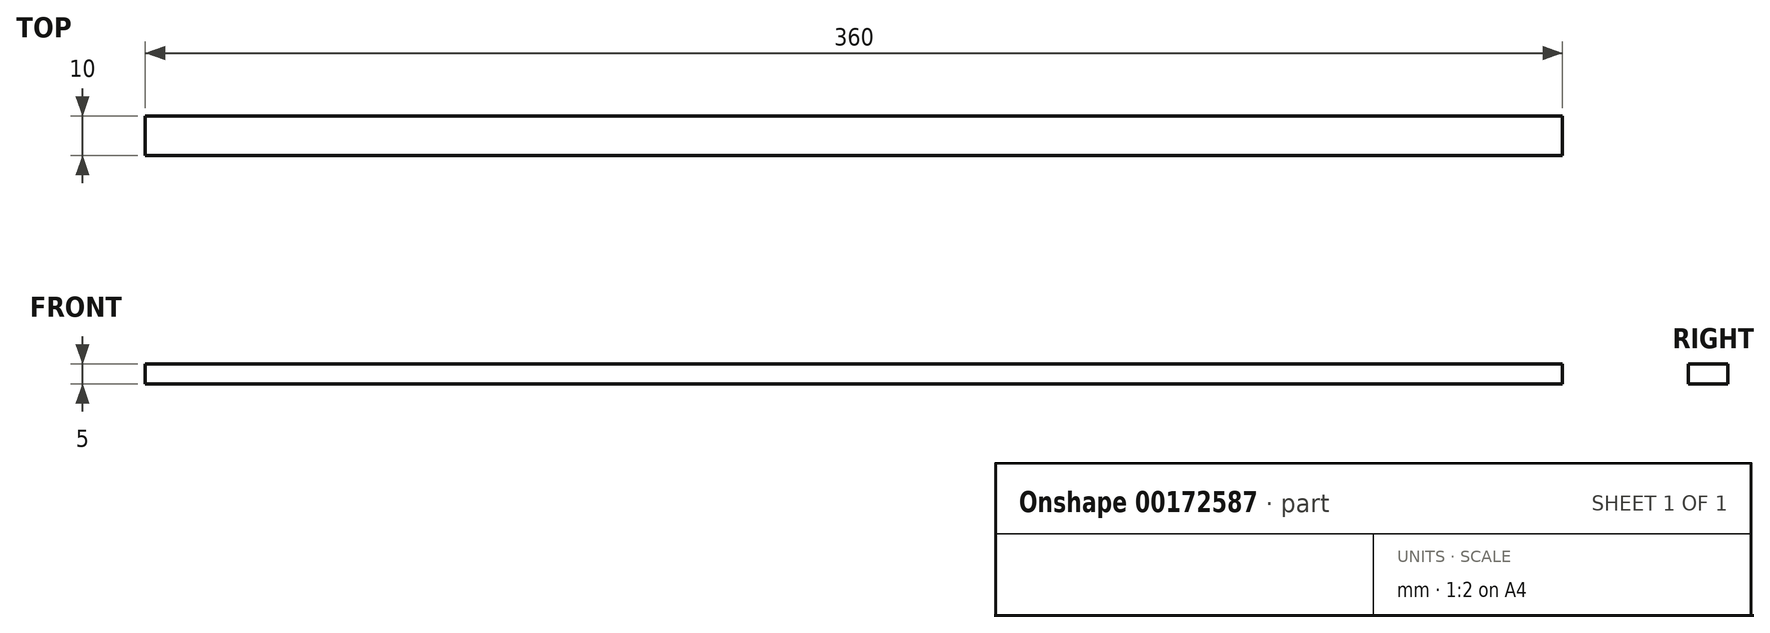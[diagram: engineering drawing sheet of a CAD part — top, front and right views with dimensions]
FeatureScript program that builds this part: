
annotation { "Feature Type Name" : "Feature", "Feature Type Description" : "" }
export const myFeature = defineFeature(function(context is Context, id is Id, definition is map)
    precondition{}
    {
        {
            var Q0;
            Q0=qCreatedBy(makeId("Right.planeOp"),FACE);
            var sketch = newSketch(context, id + "F0", { "sketchPlane" : qUnion([Q0])});
            skLineSegment(sketch, "E0.bottom", {"start": v(0, 0) * mm, "end": v(10, 0) * mm});
            skLineSegment(sketch, "E0.top", {"start": v(0, 5) * mm, "end": v(10, 5) * mm});
            skLineSegment(sketch, "E0.left", {"start": v(0, 0) * mm, "end": v(0, 5) * mm});
            skLineSegment(sketch, "E0.right", {"start": v(10, 0) * mm, "end": v(10, 5) * mm});
            skSolve(sketch);
        }
        {
            var Q0;
            Q0 = qSketchRegion(id + "F0", true);
            extrude(context, id + "F1", {"entities" : qUnion([Q0]), "depth" : 360 * mm});
        }
    });
